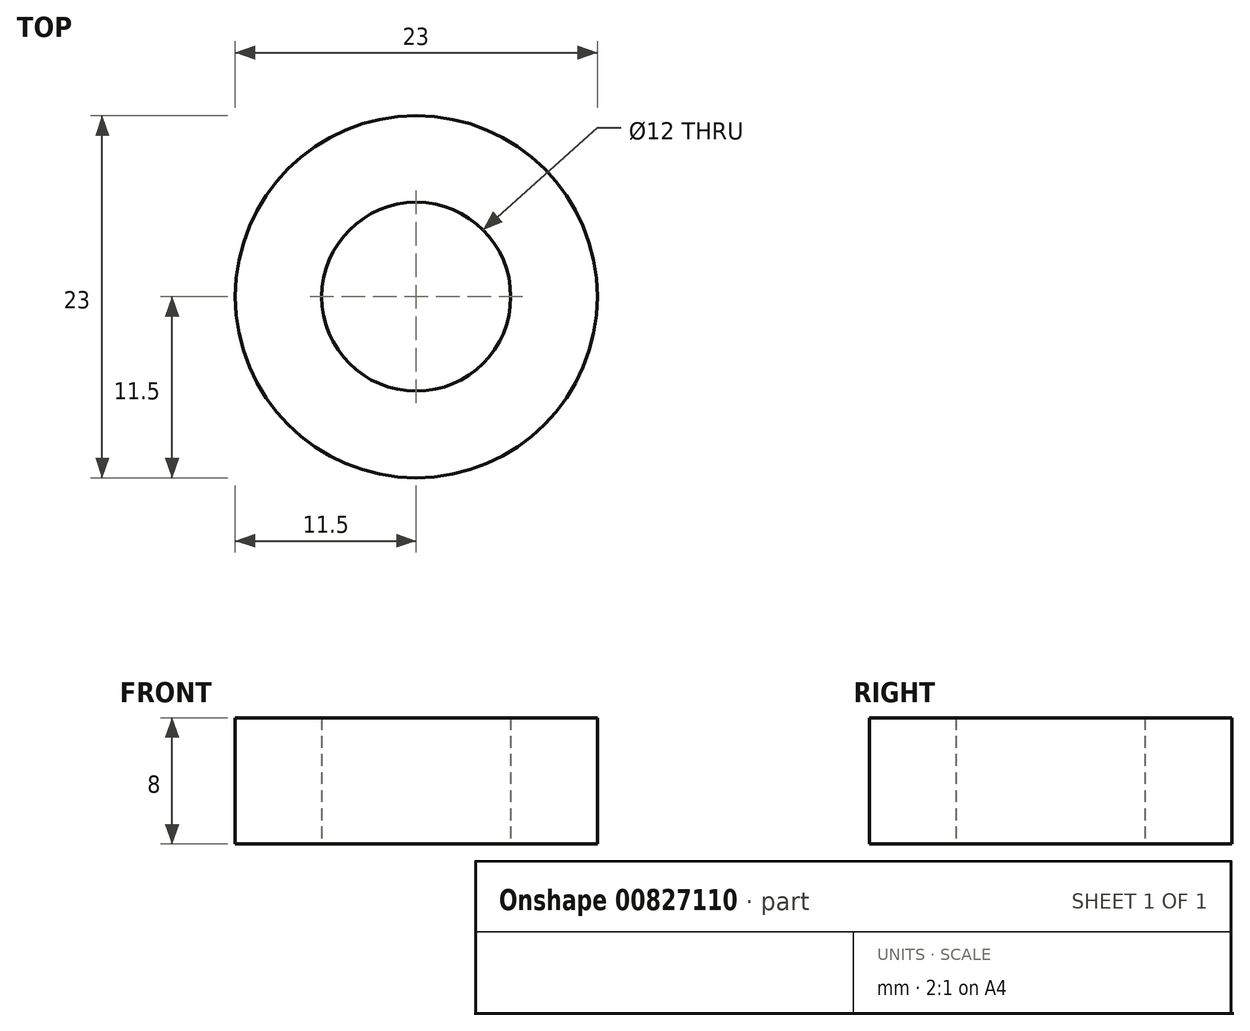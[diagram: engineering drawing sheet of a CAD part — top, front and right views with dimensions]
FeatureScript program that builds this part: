
annotation { "Feature Type Name" : "Feature", "Feature Type Description" : "" }
export const myFeature = defineFeature(function(context is Context, id is Id, definition is map)
    precondition{}
    {
        {
            var Q0;
            Q0=qCreatedBy(makeId("Top.planeOp"),FACE);
            var sketch = newSketch(context, id + "F0", { "sketchPlane" : qUnion([Q0])});
            skCircle(sketch, "E0", {"center": v(0, 0) * mm, "radius": 11.5 * mm});
            skCircle(sketch, "E1", {"center": v(0, 0) * mm, "radius": 6 * mm});
            skSolve(sketch);
        }
        {
            var Q0;
            Q0 = qSketchRegion(id + "F0", true);
            var Q1;
            Q1=makeQuery(id+"F0.imprint","IMPRINT",FACE,{"disambiguationData":[TD([[makeQuery(id+"F0.imprint","IMPRINT",EDGE,{"derivedFrom":sQuery(id+"F0.wireOp",EDGE,"E0")}),1.0]])]});
            extrude(context, id + "F1", {"entities" : qUnion([Q0, Q1]), "depth" : 8 * mm, "offsetDistance" : 25 * mm});
        }
    });
